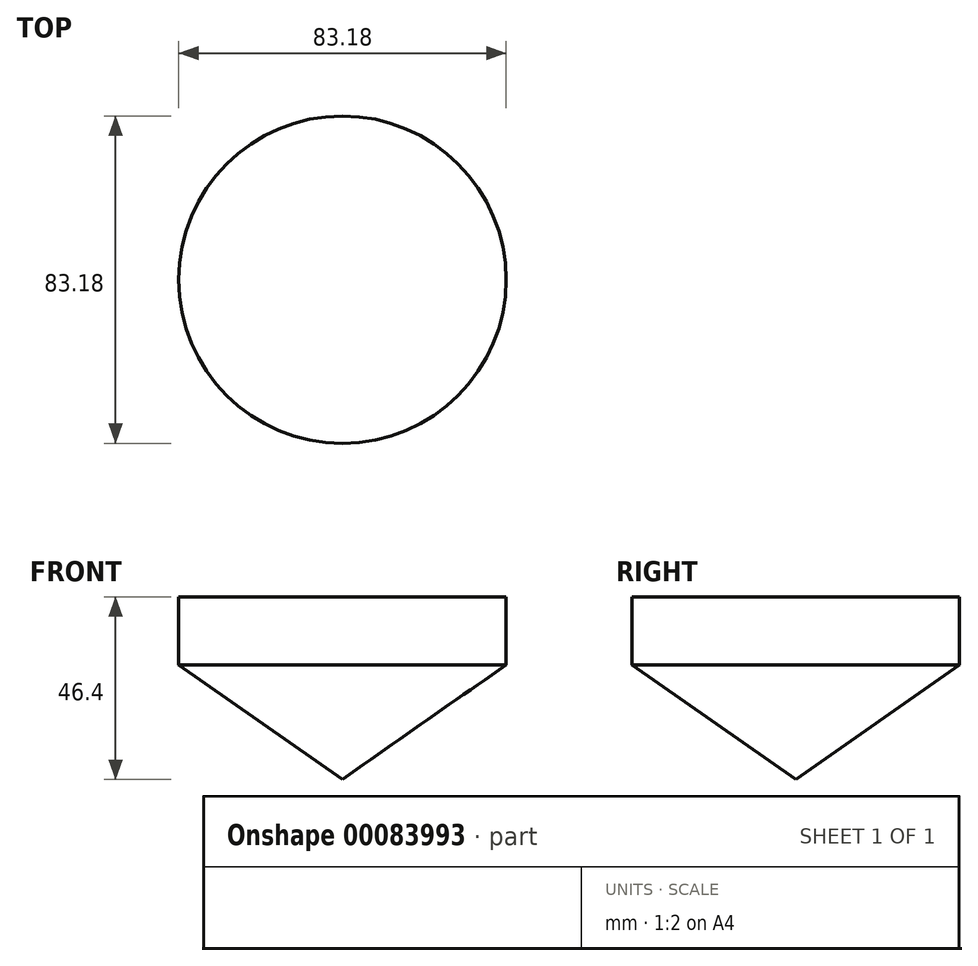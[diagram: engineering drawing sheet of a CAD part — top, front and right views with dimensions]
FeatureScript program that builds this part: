
annotation { "Feature Type Name" : "Feature", "Feature Type Description" : "" }
export const myFeature = defineFeature(function(context is Context, id is Id, definition is map)
    precondition{}
    {
        {
            var Q0;
            Q0=qCreatedBy(makeId("Front.planeOp"),FACE);
            var sketch = newSketch(context, id + "F0", { "sketchPlane" : qUnion([Q0])});
            skLineSegment(sketch, "E0", {"start": v(0, 0) * mm, "end": v(41.59, 29.17) * mm});
            skLineSegment(sketch, "E1", {"start": v(41.59, 29.17) * mm, "end": v(41.59, 46.4) * mm});
            skLineSegment(sketch, "E2", {"start": v(41.59, 46.4) * mm, "end": v(0, 46.4) * mm});
            skLineSegment(sketch, "E3", {"start": v(0, 46.4) * mm, "end": v(0, 0) * mm});
            skSolve(sketch);
        }
        {
            var Q0;
            Q0=makeQuery(id+"F0.imprint","IMPRINT",FACE,{"disambiguationData":[TD([[makeQuery(id+"F0.imprint","IMPRINT",EDGE,{"derivedFrom":sQuery(id+"F0.wireOp",EDGE,"E0")}),1.0]])]});
            var Q1;
            Q1=sQuery(id+"F0.wireOp",EDGE,"E3");
            revolve(context, id + "F1", {"entities" : qUnion([Q0]), "axis" : qUnion([Q1]), "revolveType" : RevolveType.FULL});
        }
    });
